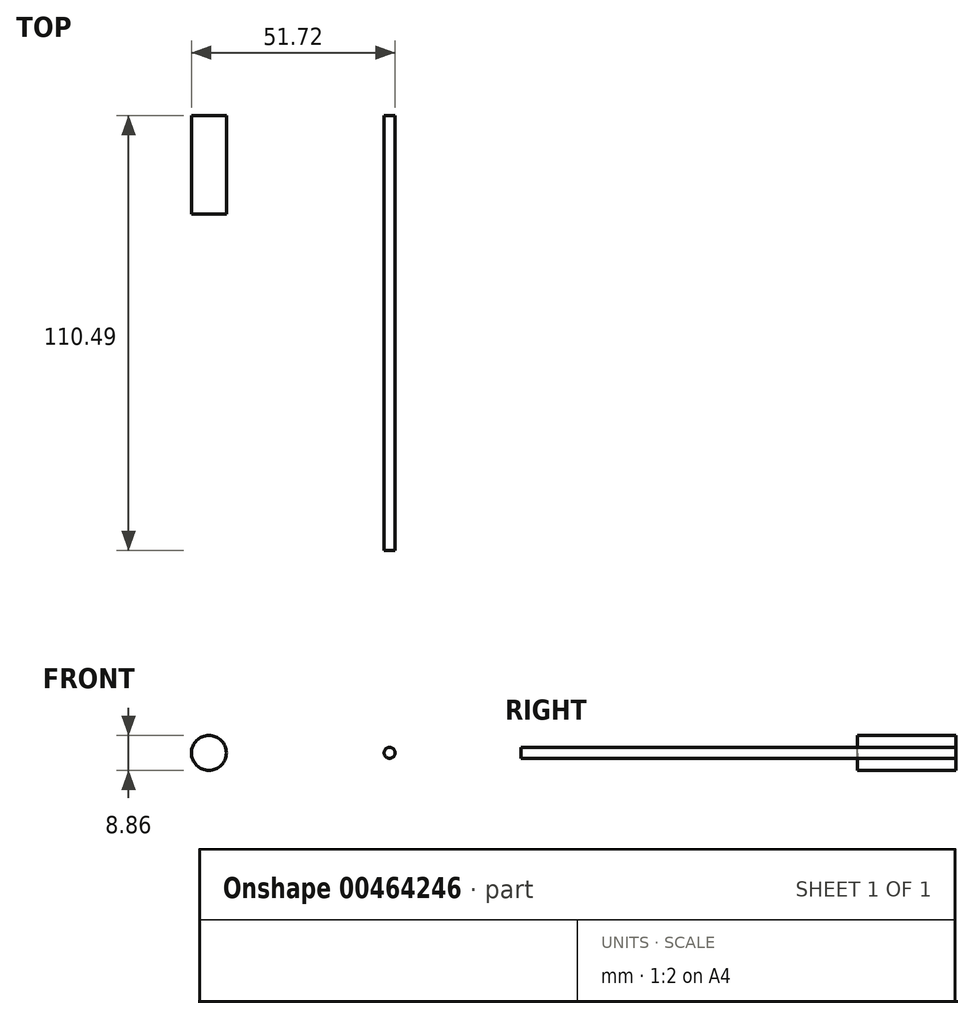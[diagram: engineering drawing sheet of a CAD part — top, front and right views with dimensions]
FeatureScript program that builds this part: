
annotation { "Feature Type Name" : "Feature", "Feature Type Description" : "" }
export const myFeature = defineFeature(function(context is Context, id is Id, definition is map)
    precondition{}
    {
        {
            var Q0;
            Q0=qCreatedBy(makeId("Front.planeOp"),FACE);
            var sketch = newSketch(context, id + "F0", { "sketchPlane" : qUnion([Q0])});
            skCircle(sketch, "E0", {"center": v(0, 0) * mm, "radius": 1.4 * mm});
            skSolve(sketch);
        }
        {
            var Q0;
            Q0=qSketchRegion(id+"F0",true);
            extrude(context, id + "F1", {"entities" : qUnion([Q0]), "depth" : 110.49 * mm});
        }
        {
            var Q0;
            Q0=qCreatedBy(makeId("Front.planeOp"),FACE);
            var sketch = newSketch(context, id + "F2", { "sketchPlane" : qUnion([Q0])});
            skCircle(sketch, "E1", {"center": v(-45.9, 0) * mm, "radius": 4.43 * mm});
            skSolve(sketch);
        }
        {
            var Q0;
            Q0=makeQuery(id+"F2.imprint","IMPRINT",FACE,{"disambiguationData":[TD([[makeQuery(id+"F2.imprint","IMPRINT",EDGE,{"derivedFrom":sQuery(id+"F2.wireOp",EDGE,"E1")}),1.0]])]});
            extrude(context, id + "F3", {"entities" : qUnion([Q0]), "depth" : 25 * mm});
        }
    });
